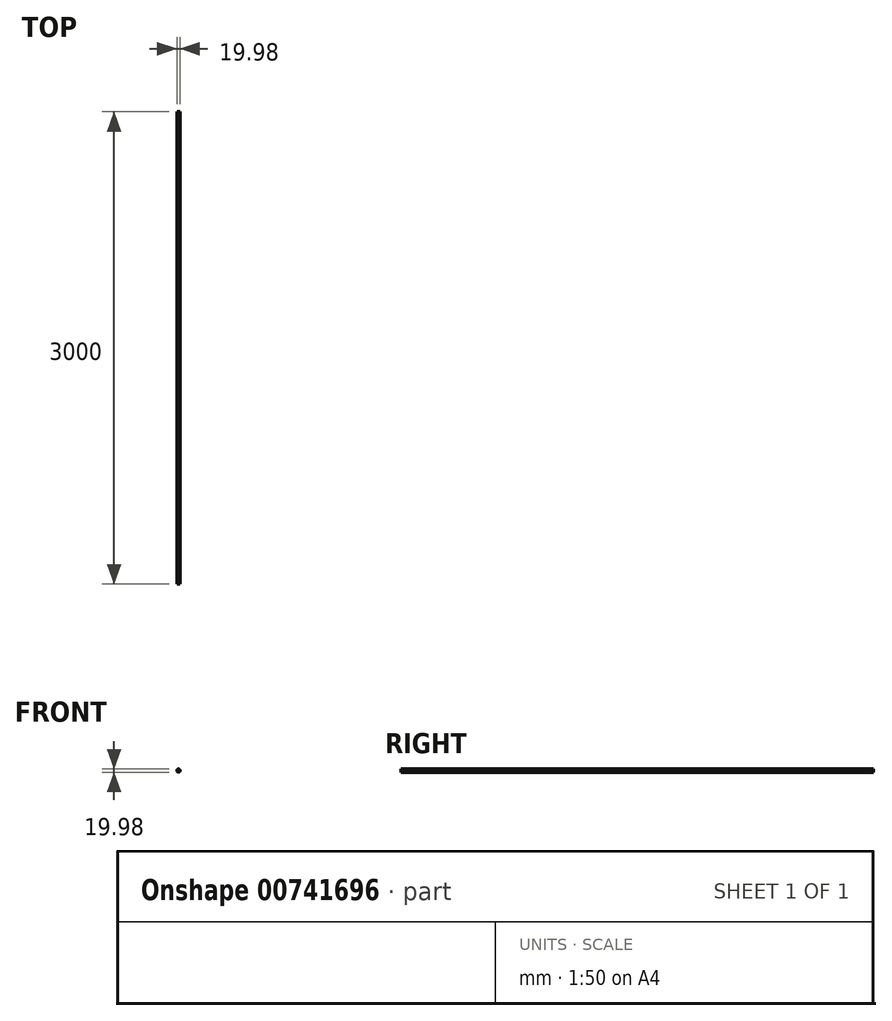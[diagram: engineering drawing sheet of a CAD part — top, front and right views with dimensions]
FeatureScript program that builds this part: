
annotation { "Feature Type Name" : "Feature", "Feature Type Description" : "" }
export const myFeature = defineFeature(function(context is Context, id is Id, definition is map)
    precondition{}
    {
        {
            var Q0;
            Q0=qCreatedBy(makeId("Front.planeOp"),FACE);
            var sketch = newSketch(context, id + "F0", { "sketchPlane" : qUnion([Q0])});
            skCircle(sketch, "E0", {"center": v(0, 0) * mm, "radius": 10 * mm});
            skSolve(sketch);
        }
        {
            var Q0;
            Q0=makeQuery(id+"F0.imprint","IMPRINT",FACE,{"disambiguationData":[TD([[makeQuery(id+"F0.imprint","IMPRINT",EDGE,{"derivedFrom":sQuery(id+"F0.wireOp",EDGE,"E0")}),1.0]])]});
            extrude(context, id + "F1", {"entities" : qUnion([Q0]), "endBound" : BoundingType.SYMMETRIC, "depth" : 3000 * mm, "offsetDistance" : 25.4 * mm});
        }
    });
